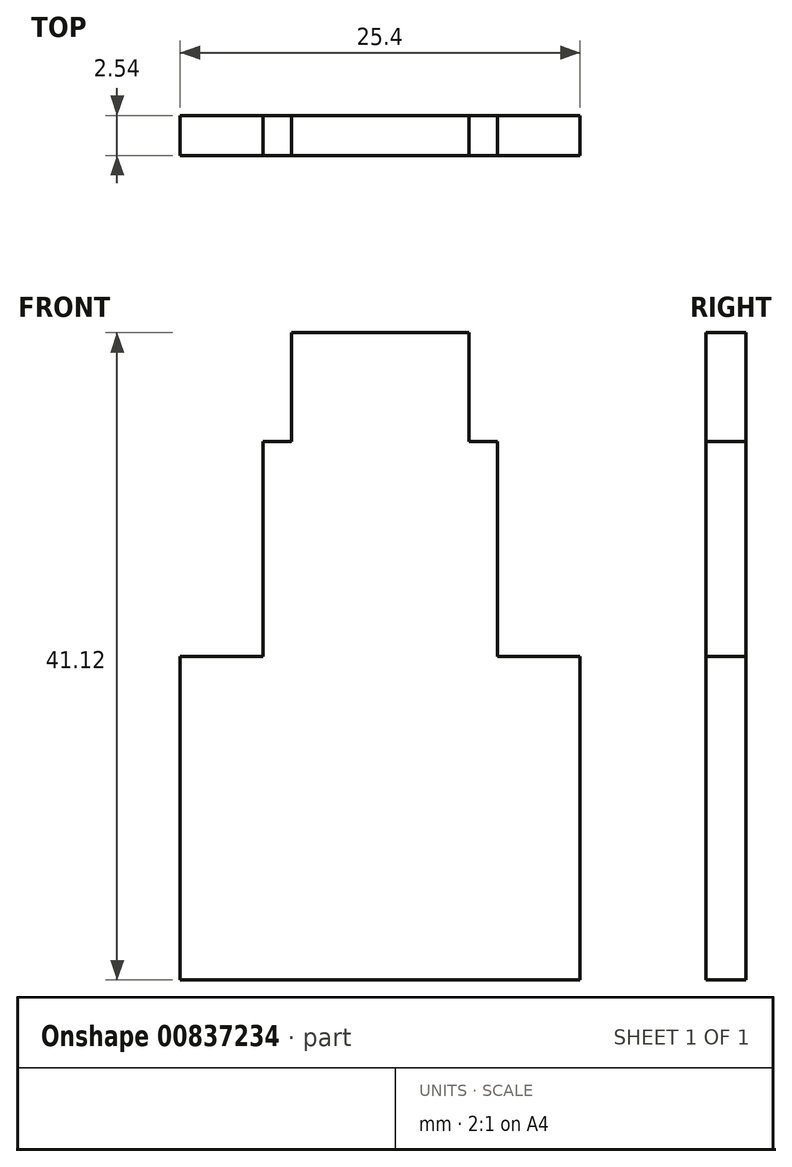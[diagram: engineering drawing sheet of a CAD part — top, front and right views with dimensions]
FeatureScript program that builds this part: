
annotation { "Feature Type Name" : "Feature", "Feature Type Description" : "" }
export const myFeature = defineFeature(function(context is Context, id is Id, definition is map)
    precondition{}
    {
        {
            var Q0;
            Q0=qCreatedBy(makeId("Front.planeOp"),FACE);
            var sketch = newSketch(context, id + "F0", { "sketchPlane" : qUnion([Q0])});
            skLineSegment(sketch, "E0", {"start": v(0, 0) * mm, "end": v(-12.7, 0) * mm});
            skLineSegment(sketch, "E1.MirrorCS", {"start": v(0, 0) * mm, "end": v(12.7, 0) * mm});
            skLineSegment(sketch, "E2", {"start": v(-12.7, 0) * mm, "end": v(-12.7, 20.55) * mm});
            skLineSegment(sketch, "E3", {"start": v(-5.63, 41.12) * mm, "end": v(5.63, 41.12) * mm});
            skLineSegment(sketch, "E4", {"start": v(12.7, 20.55) * mm, "end": v(12.7, 0) * mm});
            skLineSegment(sketch, "E5", {"start": v(-12.7, 20.55) * mm, "end": v(12.7, 20.55) * mm});
            skLineSegment(sketch, "E6", {"start": v(-7.45, 27.38) * mm, "end": v(7.45, 27.38) * mm});
            skLineSegment(sketch, "E7", {"start": v(-7.45, 34.21) * mm, "end": v(7.45, 34.21) * mm});
            skLineSegment(sketch, "E8", {"start": v(-7.45, 20.55) * mm, "end": v(-7.45, 34.21) * mm});
            skLineSegment(sketch, "E9", {"start": v(7.45, 20.55) * mm, "end": v(7.45, 34.21) * mm});
            skLineSegment(sketch, "E10", {"start": v(-5.63, 34.21) * mm, "end": v(-5.63, 41.12) * mm});
            skLineSegment(sketch, "E11", {"start": v(5.63, 34.21) * mm, "end": v(5.63, 41.12) * mm});
            skSolve(sketch);
        }
        {
            var Q0;
            Q0=makeQuery(id+"F0.imprint","IMPRINT",FACE,{"disambiguationData":[TD([[makeQuery(id+"F0.imprint","IMPRINT",EDGE,{"derivedFrom":sQuery(id+"F0.wireOp",EDGE,"E0")}),-1.0]])]});
            var Q1;
            {var subQ5=sQuery(id+"F0.wireOp",EDGE,"E6");Q1=makeQuery(id+"F0.imprint","IMPRINT",FACE,{"disambiguationData":[TD([[makeQuery(id+"F0.imprint","IMPRINT",EDGE,{"derivedFrom":subQ5}),-1.0]])]});}
            var Q2;
            {var subQ7=sQuery(id+"F0.wireOp",EDGE,"E6");Q2=makeQuery(id+"F0.imprint","IMPRINT",FACE,{"disambiguationData":[TD([[makeQuery(id+"F0.imprint","IMPRINT",EDGE,{"derivedFrom":subQ7}),1.0]])]});}
            var Q3;
            Q3=makeQuery(id+"F0.imprint","IMPRINT",FACE,{"disambiguationData":[TD([[makeQuery(id+"F0.imprint","IMPRINT",EDGE,{"derivedFrom":sQuery(id+"F0.wireOp",EDGE,"E3")}),-1.0]])]});
            extrude(context, id + "F1", {"entities" : qUnion([Q0, Q1, Q2, Q3]), "oppositeDirection" : true, "depth" : 2.54 * mm, "offsetDistance" : 25.4 * mm});
        }
    });
